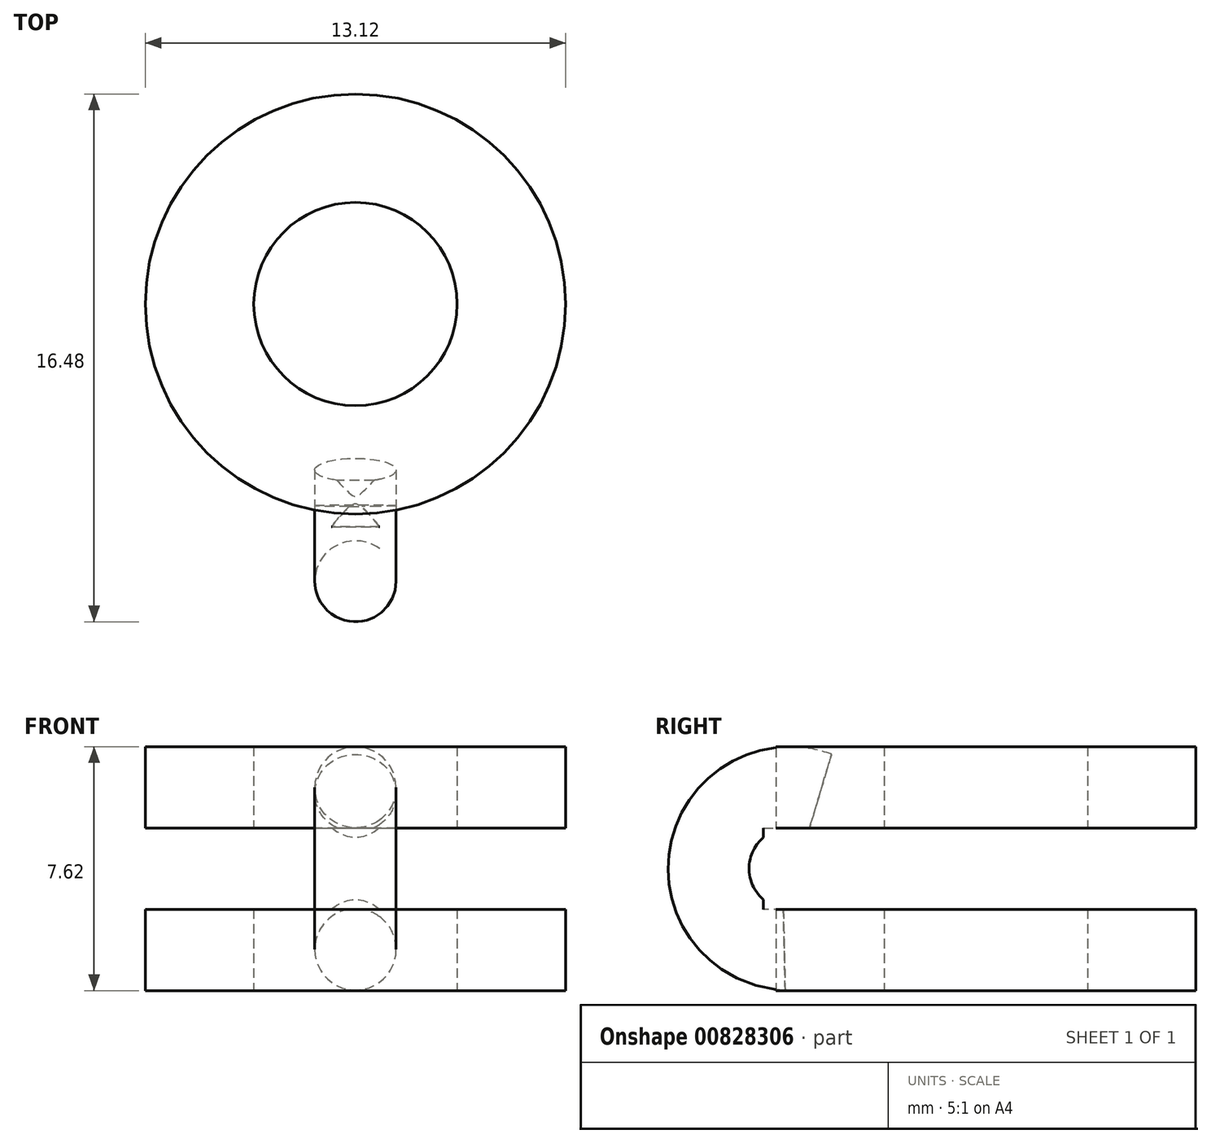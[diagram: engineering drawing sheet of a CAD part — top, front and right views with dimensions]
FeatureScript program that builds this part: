
annotation { "Feature Type Name" : "Feature", "Feature Type Description" : "" }
export const myFeature = defineFeature(function(context is Context, id is Id, definition is map)
    precondition{}
    {
        {
            var Q0;
            Q0=qCreatedBy(makeId("Top.planeOp"),FACE);
            var sketch = newSketch(context, id + "F0", { "sketchPlane" : qUnion([Q0])});
            skCircle(sketch, "E0", {"center": v(0, 0) * mm, "radius": 3.18 * mm});
            skCircle(sketch, "E1", {"center": v(0, 0) * mm, "radius": 6.56 * mm});
            skSolve(sketch);
        }
        {
            var Q0;
            Q0=makeQuery(id+"F0.imprint","IMPRINT",FACE,{"disambiguationData":[TD([[makeQuery(id+"F0.imprint","IMPRINT",EDGE,{"derivedFrom":sQuery(id+"F0.wireOp",EDGE,"E0")}),-1.0]])]});
            extrude(context, id + "F1", {"entities" : qUnion([Q0]), "depth" : 7.62 * mm, "offsetDistance" : 25.4 * mm});
        }
        {
            var Q0;
            Q0=qCreatedBy(makeId("Right.planeOp"),FACE);
            var sketch = newSketch(context, id + "F2", { "sketchPlane" : qUnion([Q0])});
            skLineSegment(sketch, "E2", {"start": v(-6.95, 25.4) * mm, "end": v(0, 25.4) * mm, "construction": true});
            skLineSegment(sketch, "E3", {"start": v(-6.95, 25.4) * mm, "end": v(-6.95, 23.04) * mm, "construction": true});
            skLineSegment(sketch, "E4", {"start": v(-6.95, 23.04) * mm, "end": v(5.75, 23.04) * mm, "construction": true});
            skLineSegment(sketch, "E5", {"start": v(-6.35, 0) * mm, "end": v(6.47, 0) * mm, "construction": true});
            skLineSegment(sketch, "E6", {"start": v(-6.35, 0) * mm, "end": v(-6.35, 2.54) * mm, "construction": true});
            skLineSegment(sketch, "E7", {"start": v(-6.35, 2.54) * mm, "end": v(7.02, 2.54) * mm, "construction": true});
            skLineSegment(sketch, "E8.bottom", {"start": v(-6.95, 5.08) * mm, "end": v(7.02, 5.08) * mm});
            skLineSegment(sketch, "E8.top", {"start": v(-6.95, 2.54) * mm, "end": v(7.02, 2.54) * mm});
            skLineSegment(sketch, "E8.left", {"start": v(-6.95, 5.08) * mm, "end": v(-6.95, 2.54) * mm});
            skLineSegment(sketch, "E8.right", {"start": v(7.02, 5.08) * mm, "end": v(7.02, 2.54) * mm});
            skSolve(sketch);
        }
        {
            var Q0;
            Q0=qCreatedBy(makeId("Front.planeOp"),FACE);
            cPlane(context, id + "F3", {"entities" : qUnion([Q0]), "cplaneType" : CPlaneType.OFFSET, "offset" : 6.35 * mm, "width" : 152.4 * mm, "height" : 152.4 * mm});
        }
        {
            var Q0;
            Q0=qCreatedBy(id+"F3.planeOp",FACE);
            var sketch = newSketch(context, id + "F4", { "sketchPlane" : qUnion([Q0])});
            skCircle(sketch, "E9", {"center": v(0, 23.56) * mm, "radius": 1.17 * mm});
            skCircle(sketch, "E10", {"center": v(0, 1.3) * mm, "radius": 1.27 * mm});
            skSolve(sketch);
        }
        {
            var Q0;
            Q0=qCreatedBy(makeId("Right.planeOp"),FACE);
            var sketch = newSketch(context, id + "F5", { "sketchPlane" : qUnion([Q0])});
            skArc(sketch, "E11", {"start": v(-4.97, 6.87) * mm, "mid": v(-9.32, 4.47) * mm, "end": v(-6.28, 0.55) * mm});
            skSolve(sketch);
        }
        {
            var Q0;
            Q0=makeQuery(id+"F4.imprint","IMPRINT",FACE,{"disambiguationData":[TD([[makeQuery(id+"F4.imprint","IMPRINT",EDGE,{"derivedFrom":sQuery(id+"F4.wireOp",EDGE,"E9")}),1.0]])]});
            var Q1;
            Q1=makeQuery(id+"F4.imprint","IMPRINT",FACE,{"disambiguationData":[TD([[makeQuery(id+"F4.imprint","IMPRINT",EDGE,{"derivedFrom":sQuery(id+"F4.wireOp",EDGE,"E10")}),1.0]])]});
            var Q2;
            Q2=sQuery(id+"F4.wireOp",EDGE,"E10");
            var Q3;
            Q3=sQuery(id+"F5.wireOp",EDGE,"E11");
            sweep(context, id + "F6", {"profiles" : qUnion([Q0, Q1]), "surfaceProfiles" : qUnion([Q2]), "path" : qUnion([Q3])});
        }
        {
            var Q0;
            Q0=makeQuery(id+"F6.opSweep","SWEPT_BODY",BODY,{"disambiguationData":[OSD([sQuery(id+"F4.wireOp",EDGE,"E9"),sQuery(id+"F5.wireOp",EDGE,"E11")])]});
            deleteBodies(context, id + "F7", {"entities" : qUnion([Q0])});
        }
        {
            var Q0;
            Q0 = qSketchRegion(id + "F2", true);
            extrude(context, id + "F8", {"entities" : qUnion([Q0]), "operationType" : NewBodyOperationType.REMOVE, "oppositeDirection" : true, "depth" : 25.4 * mm, "offsetDistance" : 25.4 * mm, "symmetric" : true});
        }
    });
